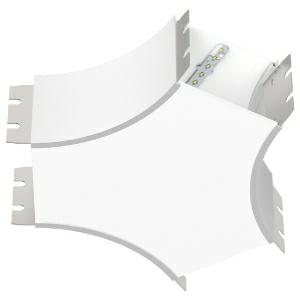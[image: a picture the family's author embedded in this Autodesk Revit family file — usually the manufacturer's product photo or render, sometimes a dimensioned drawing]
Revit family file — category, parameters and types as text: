
# Revit family: super-g_super-g_kreuzung_ab_led__8_4w_1100lm_3000k_cri_80_350-1280_4a09
name_source: partatom
category: Leuchten
revit_build: Autodesk Revit 2016 (Build: 20190508_0715(x64)
units: mm (PartAtom-declared; Revit-internal decimal feet)

## family parameters
Basisbauteil = Fläche
Beim Laden mit Abzugskörper schneiden = Nein
Bemaßung runder Anschluss = Durchmesser verwenden
Gemeinsam genutzt = Nein
Lichtquelle = Nein
Raumberechnungspunkt = Nein
Teiletyp = Normal

## types (1)
- 350-1280- (3 x LED, 480 lm, 3.3 W, 3000K)
    Approval mark = CE
    Beschreibung = The insert consists of aluminum-extruded profile. Charming SOFT-EDGE design ensure unparalleled styling. The ballast is integrated and allows for an operation with 220-240V (50/60Hz). SUPER-G (# 350-1280) ist not dimmable (on/off).
    CIE Flux Codes = 44 75 94 100 65
    Color Rendering = 1B/80…89
    Color Temperature = 3000K
    Height = 120 mm
    Hersteller = Prolicht
    Lamp Light Flux = 480 lm
    Lamp Power = 3.3 W
    Lamp count = 3
    Lampe = 3 x LED
    Length = 346 mm
    Luminous efficacy = 95 lm/W
    ModVariant = Nein
    Modell = 350-1280
    Mounting Place = Ceiling
    Mounting Type = Surface mounted
    Number of Poles = 1
    OnlyDefault = Ja
    Power Factor = 1
    Product Name = SUPER-G__SUPER-G KREUZUNG AB LED: 8,4W 1100lm 3000K CRI:80
    Product group = Surface profile systems
    ProductGroupID = 335
    Protection Class = Protection class I
    Protection Degree = IP 20
    RLX_Detail_Level = 1
    RlxData = <blob elided: 42577 chars, md5=48fbb1e8>
    Scheinlast = 10 VA
    Socket = socket
    Standby Power = 0 W
    System Light Flux = 936 lm
    System Power = 10 W
    Typenbild = 350-1280.jpg
    URL = http://relux.com
    VarID = 350-1280-
    Voltage = 0 V
    Vorgabe-Ansicht = 1800 mm
    Weight = 0.00 kg
    Width = 400 mm

## geometry (parser evidence)
native form markers: Sweep x13
no freeform markers — native parametric forms only
